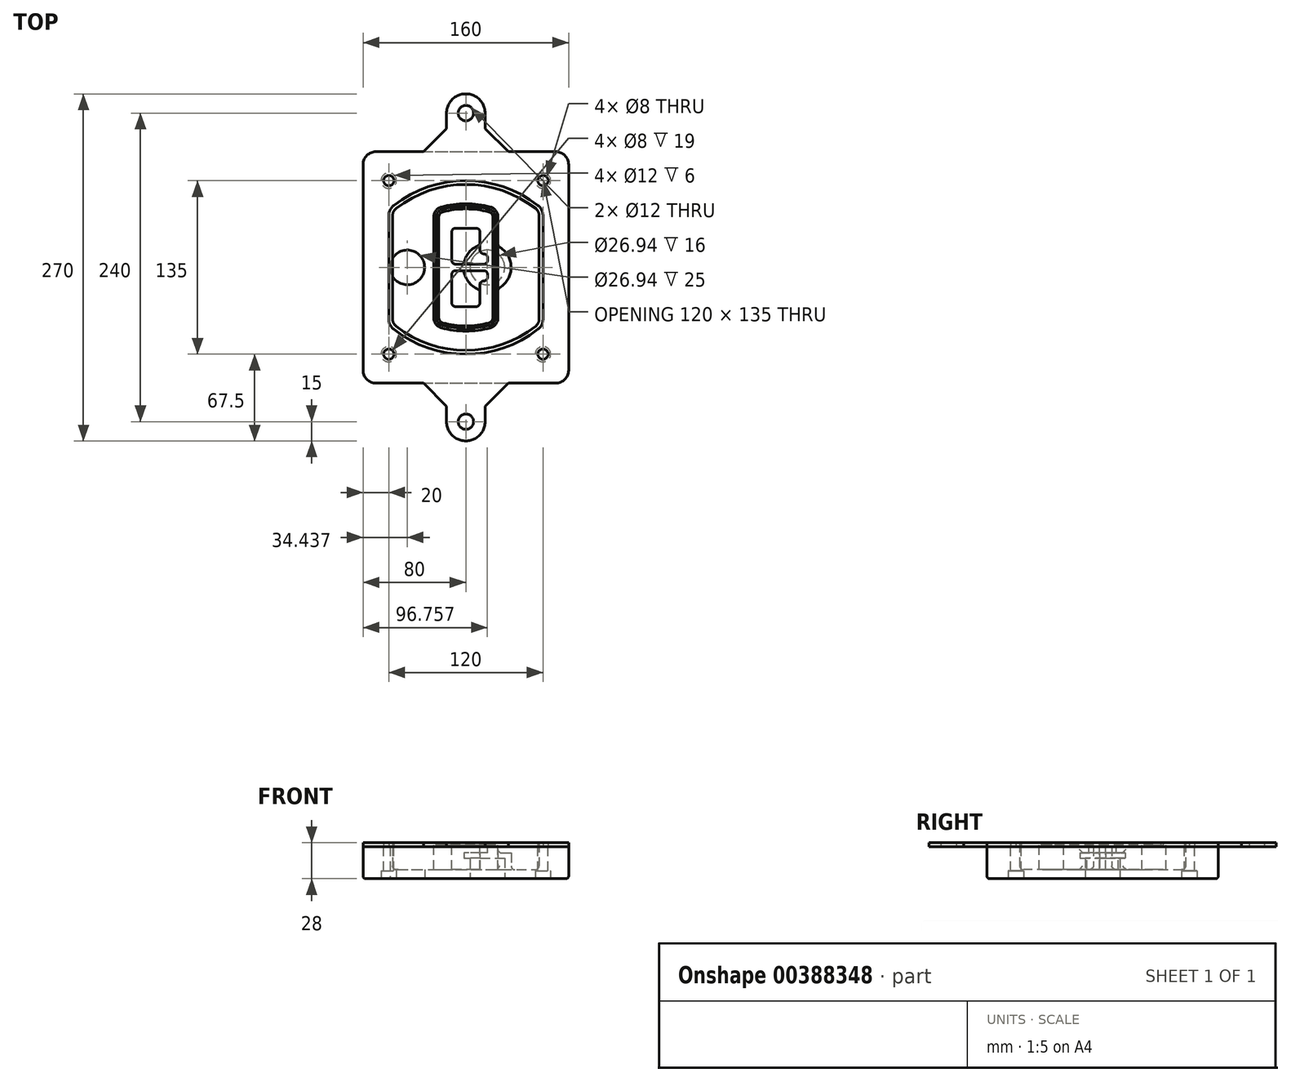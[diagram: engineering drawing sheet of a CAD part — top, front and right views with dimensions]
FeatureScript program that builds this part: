
annotation { "Feature Type Name" : "Feature", "Feature Type Description" : "" }
export const myFeature = defineFeature(function(context is Context, id is Id, definition is map)
    precondition{}
    {
        {
            var Q0;
            Q0=qCreatedBy(makeId("Top.planeOp"),FACE);
            var sketch = newSketch(context, id + "F0", { "sketchPlane" : qUnion([Q0])});
            skPoint(sketch, "E0.rect.middle", {"position": v(0, 0) * mm});
            skLineSegment(sketch, "E1.bottom", {"start": v(-70, -90) * mm, "end": v(70, -90) * mm});
            skLineSegment(sketch, "E1.top", {"start": v(-70, 90) * mm, "end": v(70, 90) * mm});
            skLineSegment(sketch, "E1.left", {"start": v(-80, -80) * mm, "end": v(-80, 80) * mm});
            skLineSegment(sketch, "E1.right", {"start": v(80, -80) * mm, "end": v(80, 80) * mm});
            skLineSegment(sketch, "E2", {"start": v(-80, 90) * mm, "end": v(80, -90) * mm, "construction": true});
            skLineSegment(sketch, "E3", {"start": v(80, 90) * mm, "end": v(-80, -90) * mm, "construction": true});
            skCircle(sketch, "E4", {"center": v(-60, 67.5) * mm, "radius": 4 * mm});
            skCircle(sketch, "E5", {"center": v(60, 67.5) * mm, "radius": 4 * mm});
            skCircle(sketch, "E6", {"center": v(60, -67.5) * mm, "radius": 4 * mm});
            skCircle(sketch, "E7", {"center": v(-60, -67.5) * mm, "radius": 4 * mm});
            skLineSegment(sketch, "E8", {"start": v(-60, 67.5) * mm, "end": v(60, 67.5) * mm, "construction": true});
            skLineSegment(sketch, "E9", {"start": v(60, 67.5) * mm, "end": v(60, -67.5) * mm, "construction": true});
            skLineSegment(sketch, "E10", {"start": v(60, -67.5) * mm, "end": v(-60, -67.5) * mm, "construction": true});
            skLineSegment(sketch, "E11", {"start": v(-60, -67.5) * mm, "end": v(-60, 67.5) * mm, "construction": true});
            skLineSegment(sketch, "E12", {"start": v(-60, 40.3) * mm, "end": v(-60, -40.3) * mm});
            skLineSegment(sketch, "E13", {"start": v(60, 40.3) * mm, "end": v(60, -40.3) * mm});
            skArc(sketch, "E14", {"start": v(56.15, 48.18) * mm, "mid": v(0, 67.5) * mm, "end": v(-56.15, 48.18) * mm});
            skArc(sketch, "E15", {"start": v(-56.15, -48.18) * mm, "mid": v(0, -67.5) * mm, "end": v(56.15, -48.18) * mm});
            skLineSegment(sketch, "E16", {"start": v(-60, 0) * mm, "end": v(60, 0) * mm, "construction": true});
            skPoint(sketch, "E17.visualSharp", {"position": v(-60, -45) * mm});
            skArc(sketch, "E17.filletArc", {"start": v(-60, -40.3) * mm, "mid": v(-58.99, -44.68) * mm, "end": v(-56.15, -48.18) * mm});
            skPoint(sketch, "E18.visualSharp", {"position": v(-60, 45) * mm});
            skArc(sketch, "E18.filletArc", {"start": v(-56.15, 48.18) * mm, "mid": v(-58.99, 44.68) * mm, "end": v(-60, 40.3) * mm});
            skPoint(sketch, "E19.visualSharp", {"position": v(60, 45) * mm});
            skArc(sketch, "E19.filletArc", {"start": v(60, 40.3) * mm, "mid": v(58.99, 44.68) * mm, "end": v(56.15, 48.18) * mm});
            skPoint(sketch, "E20.visualSharp", {"position": v(60, -45) * mm});
            skArc(sketch, "E20.filletArc", {"start": v(56.15, -48.18) * mm, "mid": v(58.99, -44.68) * mm, "end": v(60, -40.3) * mm});
            skPoint(sketch, "E21.visualSharp", {"position": v(-80, 90) * mm});
            skArc(sketch, "E21.filletArc", {"start": v(-70, 90) * mm, "mid": v(-77.07, 87.07) * mm, "end": v(-80, 80) * mm});
            skPoint(sketch, "E22.visualSharp", {"position": v(80, 90) * mm});
            skArc(sketch, "E22.filletArc", {"start": v(80, 80) * mm, "mid": v(77.07, 87.07) * mm, "end": v(70, 90) * mm});
            skPoint(sketch, "E23.visualSharp", {"position": v(80, -90) * mm});
            skArc(sketch, "E23.filletArc", {"start": v(70, -90) * mm, "mid": v(77.07, -87.07) * mm, "end": v(80, -80) * mm});
            skPoint(sketch, "E24.visualSharp", {"position": v(-80, -90) * mm});
            skArc(sketch, "E24.filletArc", {"start": v(-80, -80) * mm, "mid": v(-77.07, -87.07) * mm, "end": v(-70, -90) * mm});
            skArc(sketch, "E25.0", {"start": v(57, 40.3) * mm, "mid": v(56.3, 43.36) * mm, "end": v(54.3, 45.81) * mm});
            skLineSegment(sketch, "E25.1", {"start": v(57, 40.3) * mm, "end": v(57, -40.3) * mm});
            skArc(sketch, "E25.2", {"start": v(54.3, -45.81) * mm, "mid": v(56.3, -43.36) * mm, "end": v(57, -40.3) * mm});
            skArc(sketch, "E25.3", {"start": v(-54.3, -45.81) * mm, "mid": v(0, -64.5) * mm, "end": v(54.3, -45.81) * mm});
            skArc(sketch, "E25.4", {"start": v(-57, -40.3) * mm, "mid": v(-56.3, -43.36) * mm, "end": v(-54.3, -45.81) * mm});
            skArc(sketch, "E25.5", {"start": v(54.3, 45.81) * mm, "mid": v(0, 64.5) * mm, "end": v(-54.3, 45.81) * mm});
            skLineSegment(sketch, "E25.6", {"start": v(-57, 40.3) * mm, "end": v(-57, -40.3) * mm});
            skArc(sketch, "E25.7", {"start": v(-54.3, 45.81) * mm, "mid": v(-56.3, 43.36) * mm, "end": v(-57, 40.3) * mm});
            skArc(sketch, "E26.0", {"start": v(-58.62, 51.33) * mm, "mid": v(-62.58, 46.43) * mm, "end": v(-64, 40.3) * mm});
            skArc(sketch, "E26.1", {"start": v(58.62, 51.33) * mm, "mid": v(0, 71.5) * mm, "end": v(-58.62, 51.33) * mm});
            skArc(sketch, "E26.2", {"start": v(64, 40.3) * mm, "mid": v(62.58, 46.43) * mm, "end": v(58.62, 51.33) * mm});
            skLineSegment(sketch, "E26.3", {"start": v(64, 40.3) * mm, "end": v(64, -40.3) * mm});
            skArc(sketch, "E26.4", {"start": v(58.62, -51.33) * mm, "mid": v(62.58, -46.43) * mm, "end": v(64, -40.3) * mm});
            skLineSegment(sketch, "E26.5", {"start": v(-64, 40.3) * mm, "end": v(-64, -40.3) * mm});
            skArc(sketch, "E26.6", {"start": v(-58.62, -51.33) * mm, "mid": v(0, -71.5) * mm, "end": v(58.62, -51.33) * mm});
            skArc(sketch, "E26.7", {"start": v(-64, -40.3) * mm, "mid": v(-62.58, -46.43) * mm, "end": v(-58.62, -51.33) * mm});
            skSolve(sketch);
        }
        {
            var Q0;
            Q0=makeQuery(id+"F0.imprint","IMPRINT",FACE,{"disambiguationData":[TD([[makeQuery(id+"F0.imprint","IMPRINT",EDGE,{"derivedFrom":sQuery(id+"F0.wireOp",EDGE,"E1.bottom")}),1.0]])]});
            var Q1;
            Q1=makeQuery(id+"F0.imprint","IMPRINT",FACE,{"disambiguationData":[TD([[makeQuery(id+"F0.imprint","IMPRINT",EDGE,{"derivedFrom":sQuery(id+"F0.wireOp",EDGE,"E12")}),1.0]])]});
            var Q2;
            Q2=makeQuery(id+"F0.imprint","IMPRINT",FACE,{"disambiguationData":[TD([[makeQuery(id+"F0.imprint","IMPRINT",EDGE,{"derivedFrom":sQuery(id+"F0.wireOp",EDGE,"E25.0")}),1.0]])]});
            var Q3;
            Q3=makeQuery(id+"F0.imprint","IMPRINT",FACE,{"disambiguationData":[TD([[makeQuery(id+"F0.imprint","IMPRINT",EDGE,{"derivedFrom":sQuery(id+"F0.wireOp",EDGE,"E12")}),-1.0]])]});
            extrude(context, id + "F1", {"entities" : qUnion([Q0, Q1, Q2, Q3]), "oppositeDirection" : true, "depth" : 25 * mm});
        }
        {
            var Q0;
            Q0=makeQuery(id+"F0.imprint","IMPRINT",FACE,{"disambiguationData":[TD([[makeQuery(id+"F0.imprint","IMPRINT",EDGE,{"derivedFrom":sQuery(id+"F0.wireOp",EDGE,"E12")}),1.0]])]});
            extrude(context, id + "F2", {"entities" : qUnion([Q0]), "operationType" : NewBodyOperationType.ADD, "depth" : 3 * mm});
        }
        {
            var Q0;
            Q0=makeQuery(id+"F0.imprint","IMPRINT",FACE,{"disambiguationData":[TD([[makeQuery(id+"F0.imprint","IMPRINT",EDGE,{"derivedFrom":sQuery(id+"F0.wireOp",EDGE,"E25.0")}),1.0]])]});
            extrude(context, id + "F3", {"entities" : qUnion([Q0]), "operationType" : NewBodyOperationType.REMOVE, "oppositeDirection" : true, "depth" : 18 * mm});
        }
        {
            var Q0;
            Q0=makeQuery(id+"F2.opExtrude","CAP_FACE",FACE,{"disambiguationData":[OSD([sQuery(id+"F0.wireOp",EDGE,"E12"),sQuery(id+"F0.wireOp",EDGE,"E13"),sQuery(id+"F0.wireOp",EDGE,"E14"),sQuery(id+"F0.wireOp",EDGE,"E15"),sQuery(id+"F0.wireOp",EDGE,"E17.filletArc"),sQuery(id+"F0.wireOp",EDGE,"E18.filletArc"),sQuery(id+"F0.wireOp",EDGE,"E19.filletArc"),sQuery(id+"F0.wireOp",EDGE,"E20.filletArc"),sQuery(id+"F0.wireOp",EDGE,"E25.0"),sQuery(id+"F0.wireOp",EDGE,"E25.1"),sQuery(id+"F0.wireOp",EDGE,"E25.2"),sQuery(id+"F0.wireOp",EDGE,"E25.3"),sQuery(id+"F0.wireOp",EDGE,"E25.4"),sQuery(id+"F0.wireOp",EDGE,"E25.5"),sQuery(id+"F0.wireOp",EDGE,"E25.6"),sQuery(id+"F0.wireOp",EDGE,"E25.7")])],"isStart":false});
            var sketch = newSketch(context, id + "F4", { "sketchPlane" : qUnion([Q0])});
            skArc(sketch, "E27.0", {"start": v(-19.08, -46.97) * mm, "mid": v(0, -49.5) * mm, "end": v(19.08, -46.97) * mm});
            skArc(sketch, "E28.0", {"start": v(19.08, 46.97) * mm, "mid": v(0, 49.5) * mm, "end": v(-19.08, 46.97) * mm});
            skLineSegment(sketch, "E29", {"start": v(-25, 39.25) * mm, "end": v(-25, -39.25) * mm});
            skLineSegment(sketch, "E30", {"start": v(25, 39.25) * mm, "end": v(25, -39.25) * mm});
            skLineSegment(sketch, "E31", {"start": v(-25, 45.1) * mm, "end": v(25, 45.1) * mm, "construction": true});
            skLineSegment(sketch, "E32", {"start": v(-25, -45.1) * mm, "end": v(25, -45.1) * mm, "construction": true});
            skPoint(sketch, "E33.visualSharp", {"position": v(-25, 45.1) * mm});
            skArc(sketch, "E33.filletArc", {"start": v(-19.08, 46.97) * mm, "mid": v(-23.35, 44.11) * mm, "end": v(-25, 39.25) * mm});
            skPoint(sketch, "E34.visualSharp", {"position": v(25, 45.1) * mm});
            skArc(sketch, "E34.filletArc", {"start": v(25, 39.25) * mm, "mid": v(23.35, 44.11) * mm, "end": v(19.08, 46.97) * mm});
            skPoint(sketch, "E35.visualSharp", {"position": v(25, -45.1) * mm});
            skArc(sketch, "E35.filletArc", {"start": v(19.08, -46.97) * mm, "mid": v(23.35, -44.11) * mm, "end": v(25, -39.25) * mm});
            skPoint(sketch, "E36.visualSharp", {"position": v(-25, -45.1) * mm});
            skArc(sketch, "E36.filletArc", {"start": v(-25, -39.25) * mm, "mid": v(-23.35, -44.11) * mm, "end": v(-19.08, -46.97) * mm});
            skArc(sketch, "E37.0", {"start": v(54.3, 45.81) * mm, "mid": v(0, 64.5) * mm, "end": v(-54.3, 45.81) * mm});
            skArc(sketch, "E37.1", {"start": v(-54.3, 45.81) * mm, "mid": v(-56.3, 43.36) * mm, "end": v(-57, 40.3) * mm});
            skLineSegment(sketch, "E37.2", {"start": v(-57, 40.3) * mm, "end": v(-57, -40.3) * mm});
            skArc(sketch, "E37.3", {"start": v(-57, -40.3) * mm, "mid": v(-56.3, -43.36) * mm, "end": v(-54.3, -45.81) * mm});
            skArc(sketch, "E37.4", {"start": v(-54.3, -45.81) * mm, "mid": v(0, -64.5) * mm, "end": v(54.3, -45.81) * mm});
            skArc(sketch, "E37.5", {"start": v(54.3, -45.81) * mm, "mid": v(56.3, -43.36) * mm, "end": v(57, -40.3) * mm});
            skLineSegment(sketch, "E37.6", {"start": v(57, 40.3) * mm, "end": v(57, -40.3) * mm});
            skArc(sketch, "E37.7", {"start": v(57, 40.3) * mm, "mid": v(56.3, 43.36) * mm, "end": v(54.3, 45.81) * mm});
            skLineSegment(sketch, "E38.0", {"start": v(23, 39.25) * mm, "end": v(23, -39.25) * mm});
            skArc(sketch, "E38.1", {"start": v(18.56, -45.04) * mm, "mid": v(21.76, -42.9) * mm, "end": v(23, -39.25) * mm});
            skArc(sketch, "E38.2", {"start": v(-18.56, -45.04) * mm, "mid": v(0, -47.5) * mm, "end": v(18.56, -45.04) * mm});
            skArc(sketch, "E38.3", {"start": v(-23, -39.25) * mm, "mid": v(-21.76, -42.9) * mm, "end": v(-18.56, -45.04) * mm});
            skLineSegment(sketch, "E38.4", {"start": v(-23, 39.25) * mm, "end": v(-23, -39.25) * mm});
            skArc(sketch, "E38.5", {"start": v(23, 39.25) * mm, "mid": v(21.76, 42.9) * mm, "end": v(18.56, 45.04) * mm});
            skArc(sketch, "E38.6", {"start": v(-18.56, 45.04) * mm, "mid": v(-21.76, 42.9) * mm, "end": v(-23, 39.25) * mm});
            skArc(sketch, "E38.7", {"start": v(18.56, 45.04) * mm, "mid": v(0, 47.5) * mm, "end": v(-18.56, 45.04) * mm});
            skArc(sketch, "E39.0", {"start": v(21, 39.25) * mm, "mid": v(20.18, 41.68) * mm, "end": v(18.04, 43.1) * mm});
            skLineSegment(sketch, "E39.1", {"start": v(21, 39.25) * mm, "end": v(21, -39.25) * mm});
            skArc(sketch, "E39.2", {"start": v(18.04, -43.1) * mm, "mid": v(20.18, -41.68) * mm, "end": v(21, -39.25) * mm});
            skArc(sketch, "E39.3", {"start": v(-18.04, -43.1) * mm, "mid": v(0, -45.5) * mm, "end": v(18.04, -43.1) * mm});
            skArc(sketch, "E39.4", {"start": v(-21, -39.25) * mm, "mid": v(-20.18, -41.68) * mm, "end": v(-18.04, -43.1) * mm});
            skArc(sketch, "E39.5", {"start": v(18.04, 43.1) * mm, "mid": v(0, 45.5) * mm, "end": v(-18.04, 43.1) * mm});
            skLineSegment(sketch, "E39.6", {"start": v(-21, 39.25) * mm, "end": v(-21, -39.25) * mm});
            skArc(sketch, "E39.7", {"start": v(-18.04, 43.1) * mm, "mid": v(-20.18, 41.68) * mm, "end": v(-21, 39.25) * mm});
            skLineSegment(sketch, "E40", {"start": v(-25, 0) * mm, "end": v(25, 0) * mm, "construction": true});
            skLineSegment(sketch, "E41", {"start": v(-11, 5.5) * mm, "end": v(-11, 27.5) * mm});
            skLineSegment(sketch, "E42", {"start": v(-8, 30.5) * mm, "end": v(8, 30.5) * mm});
            skLineSegment(sketch, "E43", {"start": v(11, 27.5) * mm, "end": v(11, 13.5) * mm});
            skLineSegment(sketch, "E44", {"start": v(14, 10.5) * mm, "end": v(14, 10.5) * mm});
            skLineSegment(sketch, "E45", {"start": v(17, 7.5) * mm, "end": v(17, 5.5) * mm});
            skLineSegment(sketch, "E46", {"start": v(14, 2.5) * mm, "end": v(-8, 2.5) * mm});
            skPoint(sketch, "E47.visualSharp", {"position": v(-11, 30.5) * mm});
            skArc(sketch, "E47.filletArc", {"start": v(-8, 30.5) * mm, "mid": v(-10.12, 29.62) * mm, "end": v(-11, 27.5) * mm});
            skPoint(sketch, "E48.visualSharp", {"position": v(11, 30.5) * mm});
            skArc(sketch, "E48.filletArc", {"start": v(11, 27.5) * mm, "mid": v(10.12, 29.62) * mm, "end": v(8, 30.5) * mm});
            skPoint(sketch, "E49.visualSharp", {"position": v(11, 10.5) * mm});
            skArc(sketch, "E49.filletArc", {"start": v(11, 13.5) * mm, "mid": v(11.88, 11.38) * mm, "end": v(14, 10.5) * mm});
            skPoint(sketch, "E50.visualSharp", {"position": v(17, 10.5) * mm});
            skArc(sketch, "E50.filletArc", {"start": v(17, 7.5) * mm, "mid": v(16.12, 9.62) * mm, "end": v(14, 10.5) * mm});
            skPoint(sketch, "E51.visualSharp", {"position": v(17, 2.5) * mm});
            skArc(sketch, "E51.filletArc", {"start": v(14, 2.5) * mm, "mid": v(16.12, 3.38) * mm, "end": v(17, 5.5) * mm});
            skPoint(sketch, "E52.visualSharp", {"position": v(-11, 2.5) * mm});
            skArc(sketch, "E52.filletArc", {"start": v(-11, 5.5) * mm, "mid": v(-10.12, 3.38) * mm, "end": v(-8, 2.5) * mm});
            skLineSegment(sketch, "E53.0.MirrorCS", {"start": v(14, -2.5) * mm, "end": v(-8, -2.5) * mm});
            skArc(sketch, "E54.0.MirrorCS", {"start": v(-11, -5.5) * mm, "mid": v(-10.12, -3.38) * mm, "end": v(-8, -2.5) * mm});
            skLineSegment(sketch, "E55.0.MirrorCS", {"start": v(-11, -5.5) * mm, "end": v(-11, -27.5) * mm});
            skArc(sketch, "E56.0.MirrorCS", {"start": v(-8, -30.5) * mm, "mid": v(-10.12, -29.62) * mm, "end": v(-11, -27.5) * mm});
            skLineSegment(sketch, "E57.0.MirrorCS", {"start": v(-8, -30.5) * mm, "end": v(8, -30.5) * mm});
            skArc(sketch, "E58.0.MirrorCS", {"start": v(11, -27.5) * mm, "mid": v(10.12, -29.62) * mm, "end": v(8, -30.5) * mm});
            skLineSegment(sketch, "E59.0.MirrorCS", {"start": v(11, -27.5) * mm, "end": v(11, -13.5) * mm});
            skArc(sketch, "E60.0.MirrorCS", {"start": v(11, -13.5) * mm, "mid": v(11.88, -11.38) * mm, "end": v(14, -10.5) * mm});
            skArc(sketch, "E61.0.MirrorCS", {"start": v(17, -7.5) * mm, "mid": v(16.12, -9.62) * mm, "end": v(14, -10.5) * mm});
            skLineSegment(sketch, "E62.0.MirrorCS", {"start": v(17, -7.5) * mm, "end": v(17, -5.5) * mm});
            skArc(sketch, "E63.0.MirrorCS", {"start": v(14, -2.5) * mm, "mid": v(16.12, -3.38) * mm, "end": v(17, -5.5) * mm});
            skSolve(sketch);
        }
        {
            var Q0;
            Q0=makeQuery(id+"F4.imprint","IMPRINT",FACE,{"disambiguationData":[TD([[makeQuery(id+"F4.imprint","IMPRINT",EDGE,{"derivedFrom":sQuery(id+"F4.wireOp",EDGE,"E27.0")}),1.0]])]});
            var Q1;
            Q1=makeQuery(id+"F4.imprint","IMPRINT",FACE,{"disambiguationData":[TD([[makeQuery(id+"F4.imprint","IMPRINT",EDGE,{"derivedFrom":sQuery(id+"F4.wireOp",EDGE,"E38.0")}),-1.0]])]});
            var Q2;
            Q2=makeQuery(id+"F4.imprint","IMPRINT",FACE,{"disambiguationData":[TD([[makeQuery(id+"F4.imprint","IMPRINT",EDGE,{"derivedFrom":sQuery(id+"F4.wireOp",EDGE,"E39.0")}),1.0]])]});
            extrude(context, id + "F5", {"entities" : qUnion([Q0, Q1, Q2]), "operationType" : NewBodyOperationType.ADD, "endBound" : BoundingType.UP_TO_NEXT, "oppositeDirection" : true, "depth" : 25 * mm});
        }
        {
            var Q0;
            Q0=makeQuery(id+"F4.imprint","IMPRINT",FACE,{"disambiguationData":[TD([[makeQuery(id+"F4.imprint","IMPRINT",EDGE,{"derivedFrom":sQuery(id+"F4.wireOp",EDGE,"E38.0")}),-1.0]])]});
            extrude(context, id + "F6", {"entities" : qUnion([Q0]), "operationType" : NewBodyOperationType.REMOVE, "oppositeDirection" : true, "depth" : 2 * mm});
        }
        {
            var Q0;
            Q0=makeQuery(id+"F1.opExtrude","CAP_FACE",FACE,{"disambiguationData":[OSD([sQuery(id+"F0.wireOp",EDGE,"E1.bottom"),sQuery(id+"F0.wireOp",EDGE,"E1.top"),sQuery(id+"F0.wireOp",EDGE,"E1.left"),sQuery(id+"F0.wireOp",EDGE,"E1.right"),sQuery(id+"F0.wireOp",EDGE,"E4"),sQuery(id+"F0.wireOp",EDGE,"E5"),sQuery(id+"F0.wireOp",EDGE,"E6"),sQuery(id+"F0.wireOp",EDGE,"E7"),sQuery(id+"F0.wireOp",EDGE,"E21.filletArc"),sQuery(id+"F0.wireOp",EDGE,"E22.filletArc"),sQuery(id+"F0.wireOp",EDGE,"E23.filletArc"),sQuery(id+"F0.wireOp",EDGE,"E24.filletArc")])],"isStart":false});
            var sketch = newSketch(context, id + "F7", { "sketchPlane" : qUnion([Q0])});
            skCircle(sketch, "E64", {"center": v(16.76, 0) * mm, "radius": 13.47 * mm});
            skCircle(sketch, "E65", {"center": v(-45.56, 0) * mm, "radius": 13.47 * mm});
            skLineSegment(sketch, "E66", {"start": v(80, 0) * mm, "end": v(-80, 0) * mm});
            skCircle(sketch, "E67", {"center": v(16.76, 0) * mm, "radius": 18.47 * mm});
            skCircle(sketch, "E68", {"center": v(60, -67.5) * mm, "radius": 6 * mm});
            skCircle(sketch, "E69", {"center": v(-60, -67.5) * mm, "radius": 6 * mm});
            skCircle(sketch, "E70", {"center": v(-60, 67.5) * mm, "radius": 6 * mm});
            skCircle(sketch, "E71", {"center": v(60, 67.5) * mm, "radius": 6 * mm});
            skSolve(sketch);
        }
        {
            var Q0;
            {var subQ1=sQuery(id+"F7.wireOp",EDGE,"E66");var subQ4=sQuery(id+"F7.wireOp",EDGE,"E64");var subQ6=makeQuery(id+"F7.imprint","INTERSECT",VERTEX,{"disambiguationData":[OD(0.0)],"derivedFrom":[subQ4,subQ1]});Q0=makeQuery(id+"F7.imprint","IMPRINT",FACE,{"disambiguationData":[TD([[makeQuery(id+"F7.imprint","IMPRINT",EDGE,{"disambiguationData":[TD([[subQ6,-1.0]])],"derivedFrom":subQ4}),-1.0]])]});}
            var Q1;
            {var subQ0=sQuery(id+"F7.wireOp",EDGE,"E66");var subQ1=sQuery(id+"F7.wireOp",EDGE,"E64");var subQ3=makeQuery(id+"F7.imprint","INTERSECT",VERTEX,{"disambiguationData":[OD(0.0)],"derivedFrom":[subQ1,subQ0]});Q1=makeQuery(id+"F7.imprint","IMPRINT",FACE,{"disambiguationData":[TD([[makeQuery(id+"F7.imprint","IMPRINT",EDGE,{"disambiguationData":[TD([[subQ3,-1.0]])],"derivedFrom":subQ1}),1.0]])]});}
            var Q2;
            {var subQ0=sQuery(id+"F7.wireOp",EDGE,"E66");var subQ1=sQuery(id+"F7.wireOp",EDGE,"E64");var subQ3=makeQuery(id+"F7.imprint","INTERSECT",VERTEX,{"disambiguationData":[OD(0.0)],"derivedFrom":[subQ1,subQ0]});Q2=makeQuery(id+"F7.imprint","IMPRINT",FACE,{"disambiguationData":[TD([[makeQuery(id+"F7.imprint","IMPRINT",EDGE,{"disambiguationData":[TD([[subQ3,1.0]])],"derivedFrom":subQ1}),1.0]])]});}
            var Q3;
            {var subQ1=sQuery(id+"F7.wireOp",EDGE,"E66");var subQ4=sQuery(id+"F7.wireOp",EDGE,"E64");var subQ6=makeQuery(id+"F7.imprint","INTERSECT",VERTEX,{"disambiguationData":[OD(0.0)],"derivedFrom":[subQ4,subQ1]});Q3=makeQuery(id+"F7.imprint","IMPRINT",FACE,{"disambiguationData":[TD([[makeQuery(id+"F7.imprint","IMPRINT",EDGE,{"disambiguationData":[TD([[subQ6,1.0]])],"derivedFrom":subQ4}),-1.0]])]});}
            extrude(context, id + "F8", {"entities" : qUnion([Q0, Q1, Q2, Q3]), "operationType" : NewBodyOperationType.ADD, "oppositeDirection" : true, "depth" : 20 * mm});
        }
        {
            var Q0;
            {var subQ0=sQuery(id+"F7.wireOp",EDGE,"E66");var subQ1=sQuery(id+"F7.wireOp",EDGE,"E64");var subQ3=makeQuery(id+"F7.imprint","INTERSECT",VERTEX,{"disambiguationData":[OD(0.0)],"derivedFrom":[subQ1,subQ0]});Q0=makeQuery(id+"F7.imprint","IMPRINT",FACE,{"disambiguationData":[TD([[makeQuery(id+"F7.imprint","IMPRINT",EDGE,{"disambiguationData":[TD([[subQ3,-1.0]])],"derivedFrom":subQ1}),1.0]])]});}
            var Q1;
            {var subQ0=sQuery(id+"F7.wireOp",EDGE,"E66");var subQ1=sQuery(id+"F7.wireOp",EDGE,"E64");var subQ3=makeQuery(id+"F7.imprint","INTERSECT",VERTEX,{"disambiguationData":[OD(0.0)],"derivedFrom":[subQ1,subQ0]});Q1=makeQuery(id+"F7.imprint","IMPRINT",FACE,{"disambiguationData":[TD([[makeQuery(id+"F7.imprint","IMPRINT",EDGE,{"disambiguationData":[TD([[subQ3,1.0]])],"derivedFrom":subQ1}),1.0]])]});}
            extrude(context, id + "F9", {"entities" : qUnion([Q0, Q1]), "operationType" : NewBodyOperationType.REMOVE, "oppositeDirection" : true, "depth" : 16 * mm});
        }
        {
            var Q0;
            {var subQ0=sQuery(id+"F7.wireOp",EDGE,"E66");var subQ1=sQuery(id+"F7.wireOp",EDGE,"E65");var subQ3=makeQuery(id+"F7.imprint","INTERSECT",VERTEX,{"disambiguationData":[OD(0.0)],"derivedFrom":[subQ1,subQ0]});Q0=makeQuery(id+"F7.imprint","IMPRINT",FACE,{"disambiguationData":[TD([[makeQuery(id+"F7.imprint","IMPRINT",EDGE,{"disambiguationData":[TD([[subQ3,-1.0]])],"derivedFrom":subQ1}),1.0]])]});}
            var Q1;
            {var subQ0=sQuery(id+"F7.wireOp",EDGE,"E66");var subQ1=sQuery(id+"F7.wireOp",EDGE,"E65");var subQ3=makeQuery(id+"F7.imprint","INTERSECT",VERTEX,{"disambiguationData":[OD(0.0)],"derivedFrom":[subQ1,subQ0]});Q1=makeQuery(id+"F7.imprint","IMPRINT",FACE,{"disambiguationData":[TD([[makeQuery(id+"F7.imprint","IMPRINT",EDGE,{"disambiguationData":[TD([[subQ3,1.0]])],"derivedFrom":subQ1}),1.0]])]});}
            extrude(context, id + "F10", {"entities" : qUnion([Q0, Q1]), "operationType" : NewBodyOperationType.REMOVE, "oppositeDirection" : true, "depth" : 25 * mm});
        }
        {
            var Q0;
            Q0=makeQuery(id+"F7.imprint","IMPRINT",FACE,{"disambiguationData":[TD([[makeQuery(id+"F7.imprint","IMPRINT",EDGE,{"derivedFrom":sQuery(id+"F7.wireOp",EDGE,"E68")}),1.0]])]});
            var Q1;
            Q1=makeQuery(id+"F7.imprint","IMPRINT",FACE,{"disambiguationData":[TD([[makeQuery(id+"F7.imprint","IMPRINT",EDGE,{"derivedFrom":makeQuery(id+"F1.opExtrude","CAP_EDGE",EDGE,{"disambiguationData":[OSD([sQuery(id+"F0.wireOp",EDGE,"E5")])],"isStart":false})}),-1.0]])]});
            var Q2;
            Q2=makeQuery(id+"F7.imprint","IMPRINT",FACE,{"disambiguationData":[TD([[makeQuery(id+"F7.imprint","IMPRINT",EDGE,{"derivedFrom":sQuery(id+"F7.wireOp",EDGE,"E69")}),1.0]])]});
            var Q3;
            Q3=makeQuery(id+"F7.imprint","IMPRINT",FACE,{"disambiguationData":[TD([[makeQuery(id+"F7.imprint","IMPRINT",EDGE,{"derivedFrom":makeQuery(id+"F1.opExtrude","CAP_EDGE",EDGE,{"disambiguationData":[OSD([sQuery(id+"F0.wireOp",EDGE,"E4")])],"isStart":false})}),-1.0]])]});
            var Q4;
            Q4=makeQuery(id+"F7.imprint","IMPRINT",FACE,{"disambiguationData":[TD([[makeQuery(id+"F7.imprint","IMPRINT",EDGE,{"derivedFrom":sQuery(id+"F7.wireOp",EDGE,"E70")}),1.0]])]});
            var Q5;
            Q5=makeQuery(id+"F7.imprint","IMPRINT",FACE,{"disambiguationData":[TD([[makeQuery(id+"F7.imprint","IMPRINT",EDGE,{"derivedFrom":makeQuery(id+"F1.opExtrude","CAP_EDGE",EDGE,{"disambiguationData":[OSD([sQuery(id+"F0.wireOp",EDGE,"E7")])],"isStart":false})}),-1.0]])]});
            var Q6;
            Q6=makeQuery(id+"F7.imprint","IMPRINT",FACE,{"disambiguationData":[TD([[makeQuery(id+"F7.imprint","IMPRINT",EDGE,{"derivedFrom":sQuery(id+"F7.wireOp",EDGE,"E71")}),1.0]])]});
            var Q7;
            Q7=makeQuery(id+"F7.imprint","IMPRINT",FACE,{"disambiguationData":[TD([[makeQuery(id+"F7.imprint","IMPRINT",EDGE,{"derivedFrom":makeQuery(id+"F1.opExtrude","CAP_EDGE",EDGE,{"disambiguationData":[OSD([sQuery(id+"F0.wireOp",EDGE,"E6")])],"isStart":false})}),-1.0]])]});
            extrude(context, id + "F11", {"entities" : qUnion([Q0, Q1, Q2, Q3, Q4, Q5, Q6, Q7]), "operationType" : NewBodyOperationType.REMOVE, "oppositeDirection" : true, "depth" : 6 * mm});
        }
        {
            var Q0;
            Q0=makeQuery(id+"F9.boolean.opBoolean","COPY",FACE,{"derivedFrom":makeQuery(id+"F9.opExtrude","CAP_FACE",FACE,{"disambiguationData":[OSD([sQuery(id+"F7.wireOp",EDGE,"E64")])],"isStart":false})});
            var sketch = newSketch(context, id + "F12", { "sketchPlane" : qUnion([Q0])});
            skArc(sketch, "E72.0", {"start": v(11, 17.55) * mm, "mid": v(2.57, 11.82) * mm, "end": v(-1.54, 2.5) * mm});
            skArc(sketch, "E72.1", {"start": v(-1.54, -2.5) * mm, "mid": v(2.57, -11.82) * mm, "end": v(11, -17.55) * mm});
            skLineSegment(sketch, "E73", {"start": v(-1.54, -2.5) * mm, "end": v(14, -2.5) * mm});
            skLineSegment(sketch, "E74.0", {"start": v(14, 2.5) * mm, "end": v(-1.54, 2.5) * mm});
            skArc(sketch, "E74.1", {"start": v(14, 2.5) * mm, "mid": v(16.12, 3.38) * mm, "end": v(17, 5.5) * mm});
            skLineSegment(sketch, "E74.2", {"start": v(17, 7.5) * mm, "end": v(17, 5.5) * mm});
            skArc(sketch, "E74.3", {"start": v(17, 7.5) * mm, "mid": v(16.12, 9.62) * mm, "end": v(14, 10.5) * mm});
            skArc(sketch, "E74.4", {"start": v(11, 13.5) * mm, "mid": v(11.88, 11.38) * mm, "end": v(14, 10.5) * mm});
            skLineSegment(sketch, "E74.5", {"start": v(11, 17.55) * mm, "end": v(11, 13.5) * mm});
            skLineSegment(sketch, "E74.7", {"start": v(14, -2.5) * mm, "end": v(-1.54, -2.5) * mm});
            skArc(sketch, "E74.8", {"start": v(14, -2.5) * mm, "mid": v(16.12, -3.38) * mm, "end": v(17, -5.5) * mm});
            skLineSegment(sketch, "E74.9", {"start": v(17, -7.5) * mm, "end": v(17, -5.5) * mm});
            skArc(sketch, "E74.10", {"start": v(17, -7.5) * mm, "mid": v(16.12, -9.62) * mm, "end": v(14, -10.5) * mm});
            skArc(sketch, "E74.11", {"start": v(11, -13.5) * mm, "mid": v(11.88, -11.38) * mm, "end": v(14, -10.5) * mm});
            skLineSegment(sketch, "E74.12", {"start": v(11, -17.55) * mm, "end": v(11, -13.5) * mm});
            skPoint(sketch, "E75.orphan", {"position": v(11, -27.5) * mm});
            skPoint(sketch, "E76.orphan", {"position": v(-8, -2.5) * mm});
            skPoint(sketch, "E77.orphan", {"position": v(-8, 2.5) * mm});
            skPoint(sketch, "E78.orphan", {"position": v(11, 27.5) * mm});
            skSolve(sketch);
        }
        {
            var Q0;
            {var subQ7=sQuery(id+"F12.wireOp",EDGE,"E72.0");var subQ14=sQuery(id+"F12.wireOp",EDGE,"E72.1");var subQ16=sQuery(id+"F12.wireOp",EDGE,"E74.1");var subQ18=sQuery(id+"F12.wireOp",EDGE,"E74.8");Q0=qUnion([makeQuery(id+"F12.imprint","IMPRINT",FACE,{"disambiguationData":[TD([[makeQuery(id+"F12.imprint","IMPRINT",EDGE,{"derivedFrom":subQ7}),1.0]])]}),makeQuery(id+"F12.imprint","IMPRINT",FACE,{"disambiguationData":[TD([[makeQuery(id+"F12.imprint","IMPRINT",EDGE,{"derivedFrom":subQ14}),1.0]])]}),makeQuery(id+"F12.imprint","IMPRINT",FACE,{"disambiguationData":[TD([[makeQuery(id+"F12.imprint","IMPRINT",EDGE,{"derivedFrom":subQ16}),1.0]])]}),makeQuery(id+"F12.imprint","IMPRINT",FACE,{"disambiguationData":[TD([[makeQuery(id+"F12.imprint","IMPRINT",EDGE,{"derivedFrom":subQ18}),-1.0]])]})]);}
            var Q1;
            Q1=makeQuery(id+"F5.boolean.opBoolean","SPLIT",FACE,{"disambiguationData":[TD([makeQuery(id+"F5.opExtrude","SWEPT_FACE",FACE,{"disambiguationData":[OSD([sQuery(id+"F4.wireOp",EDGE,"E41")])]})])],"derivedFrom":makeQuery(id+"F3.boolean.opBoolean","COPY",FACE,{"derivedFrom":makeQuery(id+"F3.opExtrude","CAP_FACE",FACE,{"disambiguationData":[OSD([sQuery(id+"F0.wireOp",EDGE,"E25.0"),sQuery(id+"F0.wireOp",EDGE,"E25.1"),sQuery(id+"F0.wireOp",EDGE,"E25.2"),sQuery(id+"F0.wireOp",EDGE,"E25.3"),sQuery(id+"F0.wireOp",EDGE,"E25.4"),sQuery(id+"F0.wireOp",EDGE,"E25.5"),sQuery(id+"F0.wireOp",EDGE,"E25.6"),sQuery(id+"F0.wireOp",EDGE,"E25.7")])],"isStart":false})})});
            extrude(context, id + "F13", {"entities" : qUnion([Q0]), "operationType" : NewBodyOperationType.REMOVE, "endBound" : BoundingType.UP_TO_SURFACE, "endBoundEntityFace" : qUnion([Q1]), "depth" : 25 * mm});
        }
        {
            var Q0;
            Q0=makeQuery(id+"F3.boolean.opBoolean","COPY",EDGE,{"derivedFrom":makeQuery(id+"F3.opExtrude","CAP_EDGE",EDGE,{"disambiguationData":[OSD([sQuery(id+"F0.wireOp",EDGE,"E25.6")])],"isStart":false})});
            var Q1;
            Q1=makeQuery(id+"F8.boolean.opBoolean","INTERSECT",EDGE,{"derivedFrom":[makeQuery(id+"F5.opExtrude","SWEPT_FACE",FACE,{"disambiguationData":[OSD([sQuery(id+"F4.wireOp",EDGE,"E30")])]}),makeQuery(id+"F8.opExtrude","CAP_FACE",FACE,{"disambiguationData":[OSD([sQuery(id+"F7.wireOp",EDGE,"E67")])],"isStart":false})]});
            var Q2;
            Q2=makeQuery(id+"F8.boolean.opBoolean","INTERSECT",EDGE,{"disambiguationData":[OD(1.0)],"derivedFrom":[makeQuery(id+"F5.opExtrude","SWEPT_FACE",FACE,{"disambiguationData":[OSD([sQuery(id+"F4.wireOp",EDGE,"E30")])]}),makeQuery(id+"F8.opExtrude","SWEPT_FACE",FACE,{"disambiguationData":[OSD([sQuery(id+"F7.wireOp",EDGE,"E67")])]})]});
            var Q3;
            {var subQ0=makeQuery(id+"F3.boolean.opBoolean","COPY",FACE,{"derivedFrom":makeQuery(id+"F3.opExtrude","CAP_FACE",FACE,{"disambiguationData":[OSD([sQuery(id+"F0.wireOp",EDGE,"E25.0"),sQuery(id+"F0.wireOp",EDGE,"E25.1"),sQuery(id+"F0.wireOp",EDGE,"E25.2"),sQuery(id+"F0.wireOp",EDGE,"E25.3"),sQuery(id+"F0.wireOp",EDGE,"E25.4"),sQuery(id+"F0.wireOp",EDGE,"E25.5"),sQuery(id+"F0.wireOp",EDGE,"E25.6"),sQuery(id+"F0.wireOp",EDGE,"E25.7")])],"isStart":false})});var subQ1=sQuery(id+"F4.wireOp",EDGE,"E30");Q3=makeQuery(id+"F8.boolean.opBoolean","SPLIT",EDGE,{"disambiguationData":[TD([makeQuery(id+"F5.opExtrude","SWEPT_FACE",FACE,{"disambiguationData":[OSD([sQuery(id+"F4.wireOp",EDGE,"E35.filletArc")])]})])],"derivedFrom":makeQuery(id+"F5.opExtrude","TWEAK_EDGE",EDGE,{"derivedFrom":[subQ0,makeQuery(id+"F4.imprint","IMPRINT",EDGE,{"derivedFrom":subQ1})]})});}
            var Q4;
            {var subQ0=sQuery(id+"F0.wireOp",EDGE,"E25.0");var subQ1=sQuery(id+"F0.wireOp",EDGE,"E25.1");var subQ2=sQuery(id+"F0.wireOp",EDGE,"E25.2");var subQ3=sQuery(id+"F0.wireOp",EDGE,"E25.3");var subQ4=sQuery(id+"F0.wireOp",EDGE,"E25.4");var subQ5=sQuery(id+"F0.wireOp",EDGE,"E25.5");var subQ6=sQuery(id+"F0.wireOp",EDGE,"E25.6");var subQ7=sQuery(id+"F0.wireOp",EDGE,"E25.7");Q4=makeQuery(id+"F8.boolean.opBoolean","INTERSECT",EDGE,{"derivedFrom":[makeQuery(id+"F5.boolean.opBoolean","SPLIT",FACE,{"disambiguationData":[TD([makeQuery(id+"F2.opExtrude","SWEPT_FACE",FACE,{"disambiguationData":[OSD([subQ0])]})])],"derivedFrom":makeQuery(id+"F3.boolean.opBoolean","COPY",FACE,{"derivedFrom":makeQuery(id+"F3.opExtrude","CAP_FACE",FACE,{"disambiguationData":[OSD([subQ0,subQ1,subQ2,subQ3,subQ4,subQ5,subQ6,subQ7])],"isStart":false})})}),makeQuery(id+"F8.opExtrude","SWEPT_FACE",FACE,{"disambiguationData":[OSD([sQuery(id+"F7.wireOp",EDGE,"E67")])]})]});}
            var Q5;
            Q5=makeQuery(id+"F8.boolean.opBoolean","INTERSECT",EDGE,{"disambiguationData":[OD(0.0)],"derivedFrom":[makeQuery(id+"F5.opExtrude","SWEPT_FACE",FACE,{"disambiguationData":[OSD([sQuery(id+"F4.wireOp",EDGE,"E30")])]}),makeQuery(id+"F8.opExtrude","SWEPT_FACE",FACE,{"disambiguationData":[OSD([sQuery(id+"F7.wireOp",EDGE,"E67")])]})]});
            fillet(context, id + "F14", {"entities" : qUnion([Q0, Q1, Q2, Q3, Q4, Q5]), "radius" : 3 * mm, "tangentPropagation" : true, "allowEdgeOverflow" : false});
        }
        {
            var Q0;
            Q0=makeQuery(id+"F1.opExtrude","CAP_EDGE",EDGE,{"disambiguationData":[OSD([sQuery(id+"F0.wireOp",EDGE,"E1.bottom")])],"isStart":false});
            fillet(context, id + "F15", {"entities" : qUnion([Q0]), "radius" : 2 * mm, "tangentPropagation" : true, "allowEdgeOverflow" : false});
        }
        {
            var Q0;
            {var subQ0=sQuery(id+"F0.wireOp",EDGE,"E21.filletArc");var subQ1=sQuery(id+"F0.wireOp",EDGE,"E7");var subQ2=sQuery(id+"F0.wireOp",EDGE,"E6");var subQ3=sQuery(id+"F0.wireOp",EDGE,"E5");var subQ4=sQuery(id+"F0.wireOp",EDGE,"E4");var subQ5=sQuery(id+"F0.wireOp",EDGE,"E22.filletArc");var subQ6=sQuery(id+"F0.wireOp",EDGE,"E1.bottom");var subQ7=sQuery(id+"F0.wireOp",EDGE,"E1.right");var subQ8=sQuery(id+"F0.wireOp",EDGE,"E1.top");var subQ9=sQuery(id+"F0.wireOp",EDGE,"E1.left");var subQ10=sQuery(id+"F0.wireOp",EDGE,"E23.filletArc");var subQ11=sQuery(id+"F0.wireOp",EDGE,"E24.filletArc");Q0=makeQuery(id+"F2.boolean.opBoolean","SPLIT",FACE,{"disambiguationData":[TD([makeQuery(id+"F1.opExtrude","SWEPT_FACE",FACE,{"disambiguationData":[OSD([subQ6])]})])],"derivedFrom":makeQuery(id+"F1.opExtrude","CAP_FACE",FACE,{"disambiguationData":[OSD([subQ6,subQ8,subQ9,subQ7,subQ4,subQ3,subQ2,subQ1,subQ0,subQ5,subQ10,subQ11])],"isStart":true})});}
            var sketch = newSketch(context, id + "F16", { "sketchPlane" : qUnion([Q0])});
            skLineSegment(sketch, "E79", {"start": v(0, 90) * mm, "end": v(0, 120) * mm, "construction": true});
            skCircle(sketch, "E80", {"center": v(0, 120) * mm, "radius": 6 * mm});
            skLineSegment(sketch, "E81", {"start": v(15, 108) * mm, "end": v(33, 90) * mm});
            skLineSegment(sketch, "E82", {"start": v(-15, 108) * mm, "end": v(-33, 90) * mm});
            skArc(sketch, "E83", {"start": v(15, 119.98) * mm, "mid": v(0, 135) * mm, "end": v(-15, 119.98) * mm});
            skLineSegment(sketch, "E84", {"start": v(-15, 119.98) * mm, "end": v(-15, 108) * mm});
            skLineSegment(sketch, "E85", {"start": v(-80, 0) * mm, "end": v(80, 0) * mm, "construction": true});
            skLineSegment(sketch, "E86", {"start": v(15, 119.98) * mm, "end": v(15, 108) * mm});
            skLineSegment(sketch, "E87.MirrorCS", {"start": v(-15, -108) * mm, "end": v(-33, -90) * mm});
            skLineSegment(sketch, "E88.MirrorCS", {"start": v(-15, -119.98) * mm, "end": v(-15, -108) * mm});
            skArc(sketch, "E89.MirrorCS", {"start": v(15, -119.98) * mm, "mid": v(0, -135) * mm, "end": v(-15, -119.98) * mm});
            skCircle(sketch, "E90.MirrorC", {"center": v(0, -120) * mm, "radius": 6 * mm});
            skLineSegment(sketch, "E91.MirrorCS", {"start": v(0, -90) * mm, "end": v(0, -120) * mm, "construction": true});
            skLineSegment(sketch, "E92.MirrorCS", {"start": v(15, -119.98) * mm, "end": v(15, -108) * mm});
            skLineSegment(sketch, "E93.MirrorCS", {"start": v(15, -108) * mm, "end": v(33, -90) * mm});
            skSolve(sketch);
        }
        {
            var Q0;
            Q0=makeQuery(id+"F16.imprint","IMPRINT",FACE,{"disambiguationData":[TD([[makeQuery(id+"F16.imprint","IMPRINT",EDGE,{"derivedFrom":sQuery(id+"F16.wireOp",EDGE,"E80")}),-1.0]])]});
            var Q1;
            Q1=makeQuery(id+"F16.imprint","IMPRINT",FACE,{"disambiguationData":[TD([[makeQuery(id+"F16.imprint","IMPRINT",EDGE,{"derivedFrom":makeQuery(id+"F1.opExtrude","CAP_EDGE",EDGE,{"disambiguationData":[OSD([sQuery(id+"F0.wireOp",EDGE,"E1.left")])],"isStart":true})}),-1.0]])]});
            var Q2;
            {var subQ0=sQuery(id+"F16.wireOp",EDGE,"E87.MirrorCS");Q2=makeQuery(id+"F16.imprint","IMPRINT",FACE,{"disambiguationData":[TD([[makeQuery(id+"F16.imprint","IMPRINT",EDGE,{"derivedFrom":subQ0}),-1.0]])]});}
            var Q3;
            Q3=makeQuery(id+"F2.opExtrude","CAP_FACE",FACE,{"disambiguationData":[OSD([sQuery(id+"F0.wireOp",EDGE,"E12"),sQuery(id+"F0.wireOp",EDGE,"E13"),sQuery(id+"F0.wireOp",EDGE,"E14"),sQuery(id+"F0.wireOp",EDGE,"E15"),sQuery(id+"F0.wireOp",EDGE,"E17.filletArc"),sQuery(id+"F0.wireOp",EDGE,"E18.filletArc"),sQuery(id+"F0.wireOp",EDGE,"E19.filletArc"),sQuery(id+"F0.wireOp",EDGE,"E20.filletArc"),sQuery(id+"F0.wireOp",EDGE,"E25.0"),sQuery(id+"F0.wireOp",EDGE,"E25.1"),sQuery(id+"F0.wireOp",EDGE,"E25.2"),sQuery(id+"F0.wireOp",EDGE,"E25.3"),sQuery(id+"F0.wireOp",EDGE,"E25.4"),sQuery(id+"F0.wireOp",EDGE,"E25.5"),sQuery(id+"F0.wireOp",EDGE,"E25.6"),sQuery(id+"F0.wireOp",EDGE,"E25.7")])],"isStart":false});
            extrude(context, id + "F17", {"entities" : qUnion([Q0, Q1, Q2]), "endBound" : BoundingType.UP_TO_SURFACE, "endBoundEntityFace" : qUnion([Q3]), "depth" : 25 * mm});
        }
    });
